# Revit family: Drain_Cornice_4.5_Inch_Top-Zurn-Z182
name_source: partatom
category: Plumbing Fixtures
units: mm (PartAtom-declared; Revit-internal decimal feet)

## family parameters
Always vertical = Yes
Cut with Voids When Loaded = No
Maintain Annotation Orientation = No
OmniClass Number = 23.70.50.21.24.14
OmniClass Title = Deck Waste Water Drains
Part Type = Normal
Room Calculation Point = No
Round Connector Dimension = Use Radius
Shared = No
Work Plane-Based = No

## types (2) — shared parameters
Approx. Wt. Lbs. = 5.00 lb
Assembly Code = D2040200
Body Height (E) = 4 "
CW Connection = No
Default Elevation = 30 "
Description = 4-1/2 [114] DIAMETER CORNICE DRAIN W/ 90° OUTLET
Dome Open Area = 4.500 in²
HW Connection = No
Main Material = Iron - Zurn - Cast - Painted - Blue
Manufacturer = Zurn Water, LLC
Manufacurer Brand = Zurn
Modified Date = 01/06/2025
Pipe Size 'A' (Inner Diameter) = 2.067 "
Pipe Size 'A' (Inner Radius) = 1.034 "
Pipe Size 'A' (Nominal Diameter) = 2 "
Pipe Size 'A' (Nominal Radius) = 1 "
Pipe Size 'A' (Outer Diameter) = 2.375 "
Pipe Size 'A' (Outer Radius) = 1.188 "
Product Documentation Link = https://files.zurn.com
Product Page URL = https://www.zurn.com
Product data url = https://www.bimobject.com
URL = www.zurn.com
Vent Connection = No
WFU = 1
Waste Connection = Yes
zero-valued in all types: CWFU, HWFU

## per-type parameters (varying)
| type | Dome Material | Model |
| ZN182-2 Inch Threaded Outlet | Bronze - Zurn - Polished Nickel | ZN182 |
| ZRB182-2 Inch Threaded Outlet | Bronze - Zurn - Polished | ZRB182 |

## geometry (parser evidence)
native form markers: Blend x6, Sweep x17
no freeform markers — native parametric forms only
